# Revit family: Haworth_Planes_CollaborativeTable_Rectangular_Nested
name_source: partatom
category: Furniture Systems
revit_build: Autodesk Revit 2018 (Build: 20170223_1515(x64)
units: mm (PartAtom-declared; Revit-internal decimal feet)

## family parameters
Always vertical = No
Cut with Voids When Loaded = No
OmniClass Number = 23.40.70.14.64.21
OmniClass Title = Systems Furniture
Part Type = Normal
Room Calculation Point = No
Round Connector Dimension = Use Diameter
Shared = No
Work Plane-Based = No

## types (1)
- 60w 30d
    Actual Depth = 30"
    Actual Height = 28"
    Actual Width = 60"
    Assembly Code = E2020200
    Caster Finish = Haworth _ Paint _ Metallic Champagne
    Casters = Yes
    Custom 30 = No
    Custom 36 = Yes
    Custom Size = No
    Depth = 30"
    Description = Haworth - Planes Collaborative Table - Rectangular - Nested
    Flip Top = Yes
    Flip Top Finish = Haworth _ Paint _ Metallic Champagne
    Glides = No
    Leg Height = 26 13/16"
    Manufacturer = Haworth
    Max. Depth = 36"
    Max. Width = 72"
    Min. Depth = 25"
    Min. Width = 60"
    Min/Max Depth = 30 or 36 in.
    Min/Max Width = 60-72 in. @ 6 in. increments
    Model = Haworth - Planes Collaborative Table - Rectangular - Nested
    Revision Number = 2
    Size = Verify Final Dim. w/ Haworth
    Support Arm Depth = 2"
    Support Bar Depth = 3 1/16"
    Support Bar Thickness = 1 3/16"
    Support Spacing - From Edge = 15"
    Sustainability Info = http://www.haworth.com
    Table Thickness = 1 3/16"
    URL = www.haworth.com
    URL - Product = http://www.haworth.com
    Warranty = http://www.haworth.com
    Width = 60"

## geometry (parser evidence)
native form markers: Sweep x9
no freeform markers — native parametric forms only
